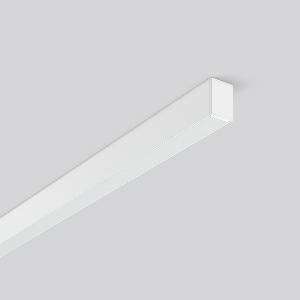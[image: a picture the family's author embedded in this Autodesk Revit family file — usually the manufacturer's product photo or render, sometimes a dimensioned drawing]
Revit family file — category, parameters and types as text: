
# Revit family: less_is_more_27_312196_002_471d
name_source: partatom
category: Lighting Fixtures
units: mm (PartAtom-declared; Revit-internal decimal feet)

## family parameters
Cut with Voids When Loaded = No
Host = Face
Light Source = No
Part Type = Normal
Room Calculation Point = No
Round Connector Dimension = Use Diameter
Shared = No

## types (1)
- LESS IS MORE 27 (1 x LED Modul 830, 1950 lm, 3000)
    Apparent Load = 29 VA
    CIE Flux Codes = 48 79 96 100 100
    Color Rendering = 80
    Color Temperature = 3000
    Default Elevation = 1800 mm
    Description = Series: LESS IS MORE 27
Ceiling and wall luminaire with slim design. Housing: extruded aluminium profile, powder-coated. End cap aluminium powder-coated. Diffuser made of non-yellowing plastic (PMMA), opal. Suitable for Ceiling mounting, Wall (surface). External driver with connecting cable. 
Colour: traffic white, matt (RAL 9016)
Length: 1012 mm
Width: 28 mm
Height: 38 mm
Lamp: LED
Socket: without socket
Colour temperature: 3000K
Colour rendering index (CRI): 82
System power: 29 W
Rated luminous flux: 1950 lm
Luminous efficiency: 67 lm/W
Control gear: Regulated power supply
Protection class: II
Type of protection: IP 20
    Height = 38 mm
    Lamp = 1 x LED Modul 830
    Lamp Light Flux = 1950 lm
    Lamp count = 1
    Length = 1012 mm
    Lifetime = 50000 h
    Luminous efficacy = 67 lm/W
    Manufacturer = RZB
    ModVariant = No
    Model = 312196.002
    Mounting Place = Ceiling, Wall
    Mounting Type = Surface mounted
    Number of Poles = 1
    OnlyDefault = Yes
    Power Factor = 1
    Product Name = LESS IS MORE 27
    Product group = Surface mounted LED linear luminaires
    ProductGroupID = 307
    Protection Class = Protection class II
    Protection Degree = IP 20
    RLX_Detail_Level = 1
    RLX_Emergency_Light_Flux = 0 lm
    RLX_Emergency_Type = 0
    RLX_Emergency_Type_DB = No
    RlxData = <blob elided: 22713 chars, md5=1f90f715>
    Socket = socket
    Standby Power = 0 W
    System Light Flux = 1950 lm
    System Power = 29 W
    Type Comments = Product without accessories
    Type Image = 312196.002.jpg
    URL = http://relux.com
    VarID = ---
    Voltage = 230 V
    Voltage Range = 220-240 V
    Weight = 0.00 kg
    Width = 28 mm

## geometry (parser evidence)
native form markers: Blend x4, Sweep x10
no freeform markers — native parametric forms only
